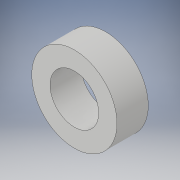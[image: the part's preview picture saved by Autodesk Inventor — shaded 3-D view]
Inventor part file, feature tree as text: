
AUTODESK INVENTOR PART (.ipt)
format: ipt  version: 2019 (Build 230136000, 136)  size: 101,888 bytes
history: native  units: mm
features: extrude x2, sketch x2
ambient origin geometry x8: Origin, YZ Plane, XZ Plane, XY Plane, X Axis, Y Axis, Z Axis, Center Point
bodies: Solid1 (feature_tree)
feature tree (4):
  extrude  "Extrusion1"  Depth=144.0mm TaperAngle=0.0deg
  extrude  "Extrusion2"  Depth=14.4mm TaperAngle=0.0deg
  sketch  "Sketch1"  dims[d0=392.0mm d1=144.0mm d2=0.0mm]
  sketch  "Sketch3"  dims[d3=224.0mm d4=14.4mm d5=0.0mm]
